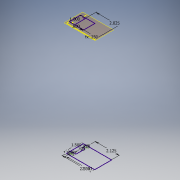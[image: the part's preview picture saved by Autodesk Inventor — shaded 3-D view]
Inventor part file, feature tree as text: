
AUTODESK INVENTOR PART (.ipt)
format: ipt  version: 2019 (Build 230136000, 136)  size: 111,104 bytes
history: native  units: in
note: dims shown in document units (in); Inventor stores cm internally (conversion verified against a paired STEP export)
features: sketch x2, plane x1
ambient origin geometry x8: Origin, YZ Plane, XZ Plane, XY Plane, X Axis, Y Axis, Z Axis, Center Point
feature tree (3):
  sketch  "Sketch5"  dims[d39=0.335in]
  plane  "Work Plane1"
  sketch  "Sketch6"  dims[d41=0.79in d42=1.5in d43=2.5in d44=0.475in d45=0.225in d46=2.313in d47=2.125in d48=10.0in d49=0.324in d50=0.238in d51=1.0in d52=0.8in d53=0.25in d58=2.025in]
